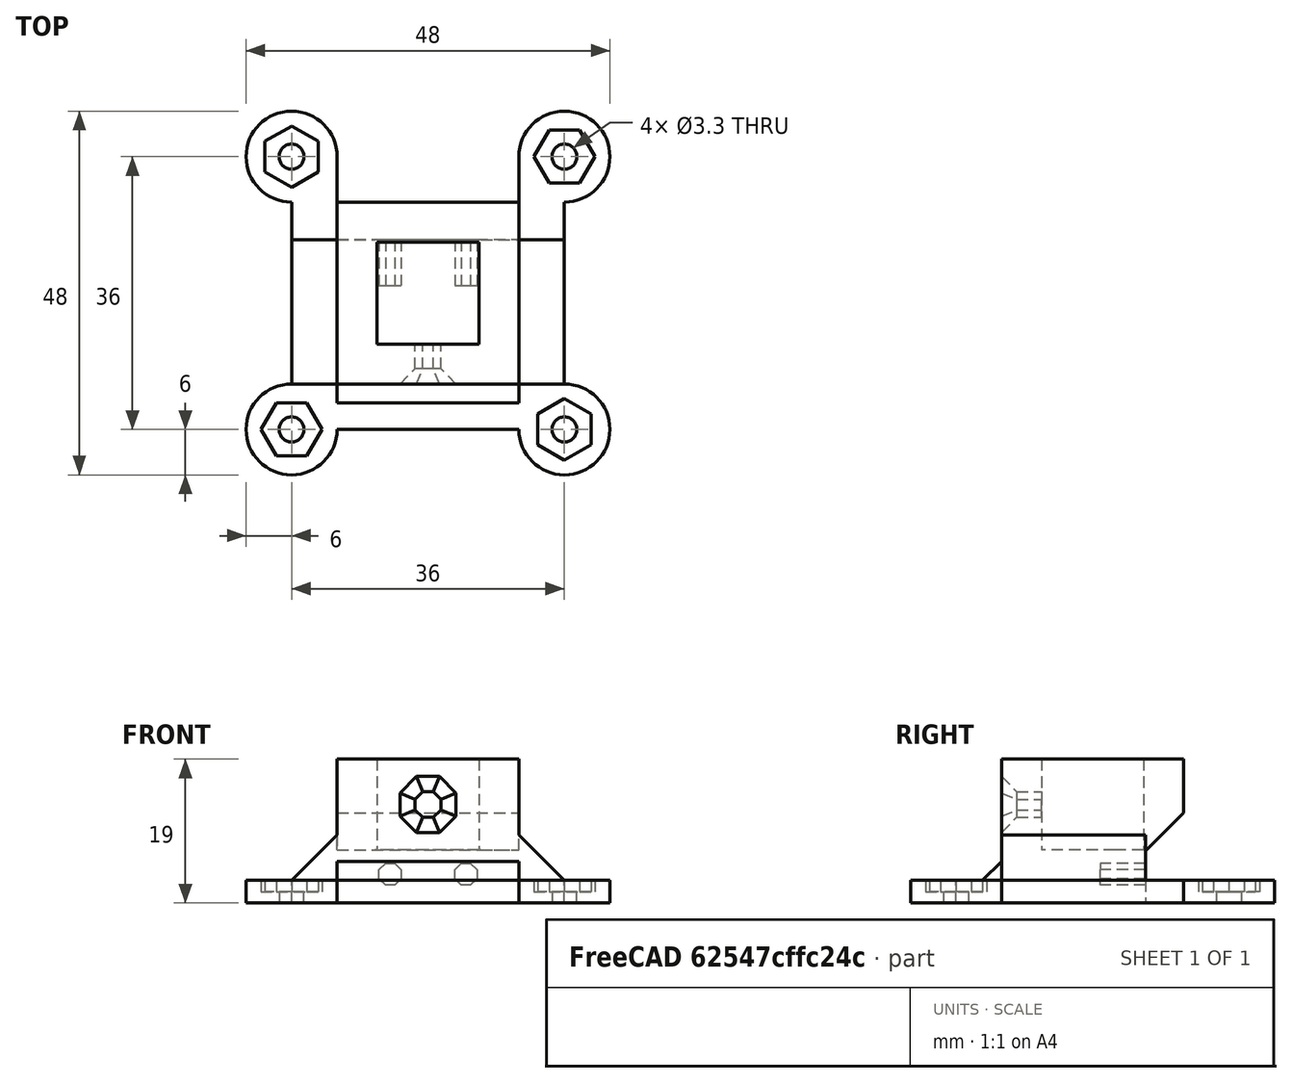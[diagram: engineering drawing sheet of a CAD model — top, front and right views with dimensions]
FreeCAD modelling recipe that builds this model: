
FCSTD DOCUMENT  (FreeCAD 0.17R13634 (Git))
Label: SG5010SquareBase V11
Comment: V6: Reinforcement at the base, following a break\n   Servo attachment octogon: 3.0 -> 3.2 mm to avoid cracks
License: CC-BY 3.0
LicenseURL: http://creativecommons.org/licenses/by/3.0/
objects: Sketcher::SketchObject×19, PartDesign::Pocket×10, PartDesign::Pad×8, PartDesign::Chamfer×5, PartDesign::Mirrored×2, PartDesign::PolarPattern×1, PartDesign::Body×1, App::Part×1
note: 64 computed .brp shape members not serialized (recipe doc carries the construction recipe); baked Part::Feature solids carry a one-line shape summary decoded from their .brp

FEATURE [Sketcher::SketchObject] Sketch  label="Base holes"
  MapMode = 5
  Support = -> [XY_Plane001]
  sketch-geometry (13):
    g0: Circle CenterX=-18 CenterY=18 CenterZ=0 NormalX=0 NormalY=0 NormalZ=1 AngleXU=0 Radius=1.65
    g1: Circle CenterX=18 CenterY=18 CenterZ=0 NormalX=0 NormalY=0 NormalZ=1 AngleXU=0 Radius=1.65
    g2: Circle CenterX=-18 CenterY=-18 CenterZ=0 NormalX=0 NormalY=0 NormalZ=1 AngleXU=0 Radius=1.65
    g3: Circle CenterX=18 CenterY=-18 CenterZ=0 NormalX=0 NormalY=0 NormalZ=1 AngleXU=0 Radius=1.65
    g4: LineSegment [constr] StartX=-18 StartY=18 StartZ=0 EndX=0 EndY=0 EndZ=0
    g5: LineSegment StartX=-12 StartY=18 StartZ=0 EndX=12 EndY=18 EndZ=0
    g6: LineSegment StartX=18 StartY=12 StartZ=0 EndX=18 EndY=-12 EndZ=0
    g7: LineSegment StartX=12 StartY=-18 StartZ=0 EndX=-12 EndY=-18 EndZ=0
    g8: LineSegment StartX=-18 StartY=-12 StartZ=0 EndX=-18 EndY=12 EndZ=0
    g9: ArcOfCircle CenterX=-18 CenterY=18 CenterZ=0 NormalX=0 NormalY=0 NormalZ=1 AngleXU=0 Radius=6 StartAngle=0 EndAngle=4.71239
    g10: ArcOfCircle CenterX=18 CenterY=18 CenterZ=0 NormalX=0 NormalY=0 NormalZ=1 AngleXU=0 Radius=6 StartAngle=4.71239 EndAngle=9.42478
    g11: ArcOfCircle CenterX=18 CenterY=-18 CenterZ=0 NormalX=0 NormalY=0 NormalZ=1 AngleXU=0 Radius=6 StartAngle=3.14159 EndAngle=7.85398
    g12: ArcOfCircle CenterX=-18 CenterY=-18 CenterZ=0 NormalX=0 NormalY=0 NormalZ=1 AngleXU=0 Radius=6 StartAngle=1.5708 EndAngle=6.28319
  constraints (35):
    c: Symmetric(g0,g1,g-2)
    c: Symmetric(g1,g3,g-1)
    c: Symmetric(g0,g2,g-1)
    c: Equal(g0,g1)
    c: Equal(g1,g3)
    c: Equal(g3,g2)
    c: Coincident(g4,g0)
    c: Coincident(g4,g-1)
    c: Angle(g4) = -0.785398
    c: Distance(g0,g1) = 36
    c: Radius(g1) = 1.65
    c: Horizontal(g5)
    c: Vertical(g6)
    c: Horizontal(g7)
    c: Vertical(g8)
    c: Coincident(g9,g5)
    c: Coincident(g9,g8)
    c: Coincident(g10,g1)
    c: Coincident(g10,g5)
    c: Coincident(g6,g10)
    c: Coincident(g11,g3)
    c: Coincident(g11,g6)
    c: Coincident(g11,g7)
    c: Coincident(g12,g2)
    c: Coincident(g7,g12)
    c: Coincident(g8,g12)
    c: Equal(g9,g10)
    c: Equal(g10,g11)
    c: Equal(g11,g12)
    c: DistanceX(g0,g8) = 0
    c: DistanceY(g7,g2) = 0
    c: DistanceX(g3,g6) = 0
    c: Coincident(g0,g9)
    c: DistanceY(g5,g0) = 0
    c: Radius(g10) = 6
FEATURE [PartDesign::Pad] Pad  label="Pad - Base holes"
  Length = 3
  Length2 = 100
  Profile = -> Sketch
  Type = 0
FEATURE [Sketcher::SketchObject] Sketch001  label="Main axis base"
  MapMode = 5
  Placement = pos=(0,0,3) rot=(0,0,1;0rad)
  Support = -> [Pad]
  sketch-geometry (4):
    g0: LineSegment StartX=-7 StartY=7 StartZ=0 EndX=7 EndY=7 EndZ=0
    g1: LineSegment StartX=7 StartY=7 StartZ=0 EndX=7 EndY=-7 EndZ=0
    g2: LineSegment StartX=7 StartY=-7 StartZ=0 EndX=-7 EndY=-7 EndZ=0
    g3: LineSegment StartX=-7 StartY=-7 StartZ=0 EndX=-7 EndY=7 EndZ=0
  constraints (12):
    c: Coincident(g0,g1)
    c: Coincident(g1,g2)
    c: Coincident(g2,g3)
    c: Coincident(g3,g0)
    c: Horizontal(g0)
    c: Horizontal(g2)
    c: Vertical(g1)
    c: Vertical(g3)
    c: Symmetric(g0,g0,g-2)
    c: Symmetric(g0,g1,g-1)
    c: Equal(g0,g1)
    c: Distance(g1) = 14
FEATURE [PartDesign::Pad] Pad001  label="Pad - Main axis base"
  BaseFeature = -> Pad
  Length = 12
  Length2 = 100
  Profile = -> Sketch001
  Type = 0
FEATURE [Sketcher::SketchObject] Sketch002  label="Main axis hole"
  MapMode = 5
  Placement = pos=(0,0,15) rot=(0,0,1;0rad)
  Support = -> [Pad001]
  sketch-geometry (1):
    g0: Circle CenterX=0 CenterY=0 CenterZ=0 NormalX=0 NormalY=0 NormalZ=1 AngleXU=0 Radius=5
  constraints (2):
    c: Coincident(g0,g-1)
    c: Radius(g0) = 5
FEATURE [PartDesign::Pocket] Pocket  label="Pocket - Main axis hole"
  BaseFeature = -> Pad001
  Length = 12
  Length2 = 100
  Profile = -> Sketch002
  Type = 0
FEATURE [Sketcher::SketchObject] Sketch003  label="Servo attachment opening"
  ExternalGeometry = -> [Pocket]
  MapMode = 5
  Placement = pos=(0,0,3) rot=(0,0,1;0rad)
  Support = -> [Pocket]
  sketch-geometry (4):
    g0: LineSegment StartX=-12 StartY=18 StartZ=0 EndX=12 EndY=18 EndZ=0
    g1: LineSegment StartX=12 StartY=18 StartZ=0 EndX=12 EndY=7 EndZ=0
    g2: LineSegment StartX=12 StartY=7 StartZ=0 EndX=-12 EndY=7 EndZ=0
    g3: LineSegment StartX=-12 StartY=7 StartZ=0 EndX=-12 EndY=18 EndZ=0
  constraints (11):
    c: Coincident(g0,g1)
    c: Coincident(g1,g2)
    c: Coincident(g2,g3)
    c: Coincident(g3,g0)
    c: Horizontal(g0)
    c: Horizontal(g2)
    c: Vertical(g1)
    c: Vertical(g3)
    c: Symmetric(g2,g1,g-2)
    c: Distance(g1) = 11
    c: Coincident(g0,g-3)
FEATURE [PartDesign::Pocket] Pocket001  label="Pocket - Servo attachment opening"
  BaseFeature = -> Pocket
  Length = 5
  Length2 = 100
  Profile = -> Sketch003
  Type = 1
FEATURE [Sketcher::SketchObject] Sketch004  label="Servo attachment wall"
  ExternalGeometry = -> [Pocket001]
  MapMode = 5
  Placement = pos=(0,7,0) rot=(0,0.707107,0.707107;3.14159rad)
  Support = -> [Pocket001]
  sketch-geometry (4):
    g0: LineSegment StartX=12 StartY=0 StartZ=0 EndX=-12 EndY=0 EndZ=0
    g1: LineSegment StartX=-12 StartY=0 StartZ=0 EndX=-12 EndY=7 EndZ=0
    g2: LineSegment StartX=-12 StartY=7 StartZ=0 EndX=12 EndY=7 EndZ=0
    g3: LineSegment StartX=12 StartY=7 StartZ=0 EndX=12 EndY=0 EndZ=0
  constraints (11):
    c: Coincident(g0,g1)
    c: Coincident(g1,g2)
    c: Coincident(g2,g3)
    c: Coincident(g3,g0)
    c: Horizontal(g0)
    c: Horizontal(g2)
    c: Vertical(g1)
    c: Vertical(g3)
    c: Coincident(g0,g-3)
    c: Coincident(g0,g-4)
    c: Distance(g1) = 7
FEATURE [PartDesign::Pad] Pad002  label="Pad - Servo attachment wall"
  BaseFeature = -> Pocket001
  Length = 2
  Length2 = 100
  Profile = -> Sketch004
  Reversed = true
  Type = 0
FEATURE [Sketcher::SketchObject] Sketch005  label="Servo attachment octogon"
  ExternalGeometry = -> [Pad002]
  MapMode = 5
  Placement = pos=(0,7,0) rot=(0,0.707107,0.707107;3.14159rad)
  Support = -> [Pad002]
  sketch-geometry (13):
    g0: LineSegment StartX=-5.66274 StartY=2.2 StartZ=0 EndX=-4.33726 EndY=2.2 EndZ=0
    g1: LineSegment StartX=-4.33726 StartY=2.2 StartZ=0 EndX=-3.4 EndY=3.13726 EndZ=0
    g2: LineSegment StartX=-3.4 StartY=3.13726 StartZ=0 EndX=-3.4 EndY=4.46274 EndZ=0
    g3: LineSegment StartX=-3.4 StartY=4.46274 StartZ=0 EndX=-4.33726 EndY=5.4 EndZ=0
    g4: LineSegment StartX=-4.33726 StartY=5.4 StartZ=0 EndX=-5.66274 EndY=5.4 EndZ=0
    g5: LineSegment StartX=-5.66274 StartY=5.4 StartZ=0 EndX=-6.6 EndY=4.46274 EndZ=0
    g6: LineSegment StartX=-6.6 StartY=4.46274 StartZ=0 EndX=-6.6 EndY=3.13726 EndZ=0
    g7: LineSegment StartX=-6.6 StartY=3.13726 StartZ=0 EndX=-5.66274 EndY=2.2 EndZ=0
    g8: LineSegment [constr] StartX=-5.66274 StartY=5.4 StartZ=0 EndX=-4.33726 EndY=2.2 EndZ=0
    g9: LineSegment [constr] StartX=-3.4 StartY=4.46274 StartZ=0 EndX=-6.6 EndY=3.13726 EndZ=0
    g10: GeomPoint [constr] X=-5 Y=3.8 Z=0
    g11: GeomPoint [constr] X=-5 Y=3.8 Z=0
    g12: GeomPoint [constr] X=5 Y=3.8 Z=0
  constraints (32):
    c: Horizontal(g0)
    c: Coincident(g0,g1)
    c: Coincident(g1,g2)
    c: Vertical(g2)
    c: Coincident(g2,g3)
    c: Coincident(g3,g4)
    c: Horizontal(g4)
    c: Coincident(g4,g5)
    c: Coincident(g5,g6)
    c: Vertical(g6)
    c: Coincident(g6,g7)
    c: Coincident(g7,g0)
    c: Equal(g5,g4)
    c: Equal(g4,g3)
    c: Equal(g3,g2)
    c: Equal(g2,g1)
    c: Equal(g1,g0)
    c: Equal(g0,g7)
    c: Equal(g7,g6)
    c: Angle(g6,g5) = 2.35619
    c: Angle(g4,g3) = 2.35619
    c: Coincident(g8,g4)
    c: Coincident(g8,g0)
    c: Coincident(g9,g2)
    c: Coincident(g9,g6)
    c: PointOnObject(g10,g8)
    c: PointOnObject(g10,g9)
    c: Distance(g5,g2) = 3.2
    c: Symmetric(g11,g12,g-2)
    c: Distance(g11,g12) = 10
    c: DistanceY(g-1,g12) = 3.8
    c: Coincident(g10,g11)
FEATURE [PartDesign::Pocket] Pocket002  label="Pocket - Servo attachment octogon"
  BaseFeature = -> Pad002
  Length = 4
  Length2 = 100
  Profile = -> Sketch005
  Type = 0
FEATURE [PartDesign::Mirrored] Mirrored
  BaseFeature = -> Pocket002
  MirrorPlane = -> Sketch005 [V_Axis]
  Originals = -> [Pocket002]
FEATURE [PartDesign::Chamfer] Chamfer
  Base = -> Mirrored [Edge55,Edge64]
  BaseFeature = -> Mirrored
  Size = 4
FEATURE [Sketcher::SketchObject] Sketch006  label="Hexagon"
  ExternalGeometry = -> [Chamfer]
  MapMode = 5
  Placement = pos=(0,0,3) rot=(0,0,1;0rad)
  Support = -> [Chamfer]
  sketch-geometry (9):
    g0: LineSegment StartX=-18 StartY=22.0415 StartZ=0 EndX=-21.5 EndY=20.0207 EndZ=0
    g1: LineSegment StartX=-21.5 StartY=20.0207 StartZ=0 EndX=-21.5 EndY=15.9793 EndZ=0
    g2: LineSegment StartX=-21.5 StartY=15.9793 StartZ=0 EndX=-18 EndY=13.9585 EndZ=0
    g3: LineSegment StartX=-18 StartY=13.9585 StartZ=0 EndX=-14.5 EndY=15.9793 EndZ=0
    g4: LineSegment StartX=-14.5 StartY=15.9793 StartZ=0 EndX=-14.5 EndY=20.0207 EndZ=0
    g5: LineSegment StartX=-14.5 StartY=20.0207 StartZ=0 EndX=-18 EndY=22.0415 EndZ=0
    g6: LineSegment [constr] StartX=-21.5 StartY=20.0207 StartZ=0 EndX=-14.5 EndY=15.9793 EndZ=0
    g7: LineSegment [constr] StartX=-14.5 StartY=20.0207 StartZ=0 EndX=-21.5 EndY=15.9793 EndZ=0
    g8: GeomPoint [constr] X=-18 Y=18 Z=0
  constraints (23):
    c: Coincident(g0,g1)
    c: Vertical(g1)
    c: Coincident(g1,g2)
    c: Coincident(g2,g3)
    c: Coincident(g3,g4)
    c: Vertical(g4)
    c: Coincident(g4,g5)
    c: Coincident(g5,g0)
    c: Equal(g0,g5)
    c: Equal(g5,g4)
    c: Equal(g4,g3)
    c: Equal(g3,g2)
    c: Equal(g2,g1)
    c: Angle(g1,g0) = 2.0944
    c: Angle(g5,g4) = 2.0944
    c: Distance(g0,g4) = 7
    c: Coincident(g6,g0)
    c: Coincident(g6,g3)
    c: Coincident(g7,g4)
    c: Coincident(g7,g1)
    c: PointOnObject(g8,g7)
    c: PointOnObject(g8,g6)
    c: Coincident(g8,g-3)
FEATURE [PartDesign::Pocket] Pocket003  label="Pocket - Hexagon"
  BaseFeature = -> Chamfer
  Length = 1.5
  Length2 = 100
  Profile = -> Sketch006
  Type = 0
FEATURE [PartDesign::PolarPattern] PolarPattern
  Angle = 360
  Axis = -> Sketch006 [N_Axis]
  BaseFeature = -> Pocket003
  Occurrences = 4
  Originals = -> [Pocket003]
FEATURE [Sketcher::SketchObject] Sketch007  label="Set screw hexagon"
  ExternalGeometry = -> [PolarPattern]
  MapMode = 5
  Placement = pos=(0,-7,0) rot=(1,0,0;1.5708rad)
  Support = -> [PolarPattern]
  sketch-geometry (14):
    g0: LineSegment [constr] StartX=-7 StartY=15 StartZ=0 EndX=7 EndY=3 EndZ=0
    g1: LineSegment [constr] StartX=-7 StartY=3 StartZ=0 EndX=7 EndY=15 EndZ=0
    g2: GeomPoint [constr] X=0 Y=9 Z=0
    g3: LineSegment StartX=-1.65 StartY=9.68345 StartZ=0 EndX=-1.65 EndY=8.31655 EndZ=0
    g4: LineSegment StartX=-1.65 StartY=8.31655 StartZ=0 EndX=-0.683452 EndY=7.35 EndZ=0
    g5: LineSegment StartX=-0.683452 StartY=7.35 StartZ=0 EndX=0.683452 EndY=7.35 EndZ=0
    g6: LineSegment StartX=0.683452 StartY=7.35 StartZ=0 EndX=1.65 EndY=8.31655 EndZ=0
    g7: LineSegment StartX=1.65 StartY=8.31655 StartZ=0 EndX=1.65 EndY=9.68345 EndZ=0
    g8: LineSegment StartX=1.65 StartY=9.68345 StartZ=0 EndX=0.683452 EndY=10.65 EndZ=0
    g9: LineSegment StartX=0.683452 StartY=10.65 StartZ=0 EndX=-0.683452 EndY=10.65 EndZ=0
    g10: LineSegment StartX=-0.683452 StartY=10.65 StartZ=0 EndX=-1.65 EndY=9.68345 EndZ=0
    g11: LineSegment [constr] StartX=-0.683452 StartY=10.65 StartZ=0 EndX=0.683452 EndY=7.35 EndZ=0
    g12: LineSegment [constr] StartX=1.65 StartY=9.68345 StartZ=0 EndX=-1.65 EndY=8.31655 EndZ=0
    g13: GeomPoint [constr] X=0 Y=9 Z=0
  constraints (35):
    c: Coincident(g0,g-3)
    c: Coincident(g0,g-4)
    c: Coincident(g1,g-3)
    c: Coincident(g1,g-4)
    c: PointOnObject(g2,g1)
    c: PointOnObject(g2,g0)
    c: Vertical(g3)
    c: Coincident(g3,g4)
    c: Coincident(g4,g5)
    c: Horizontal(g5)
    c: Coincident(g5,g6)
    c: Coincident(g6,g7)
    c: Vertical(g7)
    c: Coincident(g7,g8)
    c: Coincident(g8,g9)
    c: Horizontal(g9)
    c: Coincident(g9,g10)
    c: Coincident(g10,g3)
    c: Equal(g10,g9)
    c: Equal(g9,g8)
    c: Equal(g8,g7)
    c: Equal(g7,g6)
    c: Equal(g6,g5)
    c: Equal(g5,g4)
    c: Equal(g4,g3)
    c: Angle(g10,g9) = 2.35619
    c: Angle(g8,g7) = 2.35619
    c: Coincident(g11,g9)
    c: Coincident(g11,g5)
    c: Coincident(g12,g7)
    c: Coincident(g12,g3)
    c: PointOnObject(g13,g12)
    c: PointOnObject(g13,g11)
    c: Distance(g3,g7) = 3.3
    c: Coincident(g13,g2)
FEATURE [PartDesign::Pocket] Pocket004  label="Pocket - Set screw hexagon"
  BaseFeature = -> PolarPattern
  Length = 5
  Length2 = 100
  Profile = -> Sketch007
  Type = 0
FEATURE [PartDesign::Chamfer] Chamfer001
  Base = -> Pocket004 [Edge147,Edge60,Edge67,Edge66,Edge65,Edge64,Edge63,Edge62,Edge61]
  BaseFeature = -> Pocket004
  Size = 1
FEATURE [Sketcher::SketchObject] Sketch008  label="Rectangular base enlargement"
  ExternalGeometry = -> [Chamfer001]
  MapMode = 5
  Placement = pos=(7,0,0) rot=(0.57735,0.57735,0.57735;2.0944rad)
  Support = -> [Chamfer001]
  sketch-geometry (8):
    g0: LineSegment StartX=-7 StartY=7 StartZ=0 EndX=-12 EndY=7 EndZ=0
    g1: LineSegment StartX=-12 StartY=7 StartZ=0 EndX=-12 EndY=-12 EndZ=0
    g2: LineSegment StartX=-12 StartY=-12 StartZ=0 EndX=12 EndY=-12 EndZ=0
    g3: LineSegment StartX=12 StartY=-12 StartZ=0 EndX=12 EndY=7 EndZ=0
    g4: LineSegment StartX=12 StartY=7 StartZ=0 EndX=7 EndY=7 EndZ=0
    g5: LineSegment StartX=7 StartY=7 StartZ=0 EndX=7 EndY=-7 EndZ=0
    g6: LineSegment StartX=7 StartY=-7 StartZ=0 EndX=-7 EndY=-7 EndZ=0
    g7: LineSegment StartX=-7 StartY=-7 StartZ=0 EndX=-7 EndY=7 EndZ=0
  constraints (19):
    c: Coincident(g-3,g0)
    c: Coincident(g0,g1)
    c: Vertical(g1)
    c: Coincident(g1,g2)
    c: Horizontal(g2)
    c: Coincident(g2,g3)
    c: Vertical(g3)
    c: Coincident(g3,g4)
    c: Coincident(g4,g-4)
    c: Horizontal(g4)
    c: Coincident(g4,g5)
    c: Coincident(g5,g-4)
    c: Coincident(g5,g6)
    c: Coincident(g6,g-3)
    c: Coincident(g6,g7)
    c: Coincident(g7,g0)
    c: Symmetric(g0,g3,g-2)
    c: Coincident(g3,g-5)
    c: Distance(g3) = 19
FEATURE [PartDesign::Pad] Pad003  label="Pad - Rectangular base enlargement"
  BaseFeature = -> Chamfer001
  Length = 15
  Length2 = 100
  Profile = -> Sketch008
  Reversed = true
  Type = 0
FEATURE [Sketcher::SketchObject] Sketch009  label="Window to set screw"
  ExternalGeometry = -> [Pad003]
  MapMode = 5
  Placement = pos=(7,0,0) rot=(0.57735,0.57735,0.57735;2.0944rad)
  Support = -> [Pad003]
  sketch-geometry (10):
    g0: LineSegment [constr] StartX=-12 StartY=15 StartZ=0 EndX=12 EndY=3 EndZ=0
    g1: LineSegment [constr] StartX=-12 StartY=3 StartZ=0 EndX=12 EndY=15 EndZ=0
    g2: GeomPoint [constr] X=0 Y=9 Z=0
    g3: LineSegment StartX=-3.25 StartY=12.25 StartZ=0 EndX=3.25 EndY=12.25 EndZ=0
    g4: LineSegment StartX=3.25 StartY=12.25 StartZ=0 EndX=3.25 EndY=5.75 EndZ=0
    g5: LineSegment StartX=3.25 StartY=5.75 StartZ=0 EndX=-3.25 EndY=5.75 EndZ=0
    g6: LineSegment StartX=-3.25 StartY=5.75 StartZ=0 EndX=-3.25 EndY=12.25 EndZ=0
    g7: LineSegment [constr] StartX=-3.25 StartY=12.25 StartZ=0 EndX=3.25 EndY=5.75 EndZ=0
    g8: LineSegment [constr] StartX=3.25 StartY=12.25 StartZ=0 EndX=-3.25 EndY=5.75 EndZ=0
    g9: GeomPoint [constr] X=0 Y=9 Z=0
  constraints (23):
    c: Coincident(g0,g-4)
    c: Coincident(g0,g-3)
    c: Coincident(g1,g-4)
    c: Coincident(g1,g-3)
    c: PointOnObject(g2,g1)
    c: PointOnObject(g2,g0)
    c: Coincident(g3,g4)
    c: Coincident(g4,g5)
    c: Coincident(g5,g6)
    c: Coincident(g6,g3)
    c: Horizontal(g3)
    c: Horizontal(g5)
    c: Vertical(g4)
    c: Vertical(g6)
    c: Coincident(g7,g4)
    c: Coincident(g7,g3)
    c: Coincident(g8,g3)
    c: Coincident(g8,g5)
    c: PointOnObject(g9,g7)
    c: PointOnObject(g9,g8)
    c: Coincident(g9,g2)
    c: Equal(g3,g4)
    c: Distance(g3) = 6.5
FEATURE [PartDesign::Pocket] Pocket005
  BaseFeature = -> Pad003
  Length = 5
  Length2 = 100
  Profile = -> Sketch009
  Type = 0
FEATURE [PartDesign::Chamfer] Chamfer002
  Base = -> Pocket005 [Edge110]
  BaseFeature = -> Pocket005
  Size = 2.5
FEATURE [Sketcher::SketchObject] Sketch010  label="Side reinforcement triangle"
  ExternalGeometry = -> [Chamfer002]
  MapMode = 5
  Placement = pos=(0,7,0) rot=(0,0.707107,0.707107;3.14159rad)
  Support = -> [Chamfer002]
  sketch-geometry (3):
    g0: LineSegment StartX=12 StartY=9 StartZ=0 EndX=12 EndY=3 EndZ=0
    g1: LineSegment StartX=12 StartY=3 StartZ=0 EndX=18 EndY=3 EndZ=0
    g2: LineSegment StartX=18 StartY=3 StartZ=0 EndX=12 EndY=9 EndZ=0
  constraints (9):
    c: Vertical(g0)
    c: Coincident(g0,g1)
    c: Horizontal(g1)
    c: Coincident(g1,g2)
    c: Coincident(g2,g0)
    c: PointOnObject(g0,g-3)
    c: Coincident(g-4,g0)
    c: Distance(g1) = 6
    c: Equal(g0,g1)
FEATURE [PartDesign::Pad] Pad004  label="Pad - Side reinforcement triangle"
  BaseFeature = -> Chamfer002
  Length = 19
  Length2 = 100
  Profile = -> Sketch010
  Reversed = true
  Type = 0
FEATURE [PartDesign::Mirrored] Mirrored001
  BaseFeature = -> Pad004
  MirrorPlane = -> Sketch010 [V_Axis]
  Originals = -> [Pad004]
FEATURE [Sketcher::SketchObject] Sketch011
  MapMode = 5
  Support = -> [XY_Plane001]
FEATURE [Sketcher::SketchObject] Sketch012  label="Shave_top"
  ExternalGeometry = -> [Mirrored001]
  MapMode = 5
  Placement = pos=(0,7,0) rot=(0,0.707107,0.707107;3.14159rad)
  Support = -> [Mirrored001]
  sketch-geometry (4):
    g0: LineSegment StartX=-12 StartY=15 StartZ=0 EndX=12 EndY=15 EndZ=0
    g1: LineSegment StartX=12 StartY=15 StartZ=0 EndX=12 EndY=7 EndZ=0
    g2: LineSegment StartX=12 StartY=7 StartZ=0 EndX=-12 EndY=7 EndZ=0
    g3: LineSegment StartX=-12 StartY=7 StartZ=0 EndX=-12 EndY=15 EndZ=0
  constraints (10):
    c: Coincident(g0,g1)
    c: Coincident(g1,g2)
    c: Coincident(g2,g3)
    c: Coincident(g3,g0)
    c: Horizontal(g0)
    c: Horizontal(g2)
    c: Vertical(g1)
    c: Vertical(g3)
    c: Coincident(g-5,g0)
    c: Coincident(g1,g-6)
FEATURE [PartDesign::Pocket] Pocket006
  BaseFeature = -> Mirrored001
  Length = 5
  Length2 = 100
  Profile = -> Sketch012
  Type = 1
FEATURE [Sketcher::SketchObject] Sketch013  label="Fill_holes"
  ExternalGeometry = -> [Pocket006]
  MapMode = 5
  Placement = pos=(0,0,7) rot=(0,0,1;0rad)
  Support = -> [Pocket006]
  sketch-geometry (8):
    g0: LineSegment StartX=-4.4828 StartY=3.78315 StartZ=0 EndX=-1.67 EndY=5.48969 EndZ=0
    g1: LineSegment StartX=-1.67 StartY=5.48969 StartZ=0 EndX=1.67 EndY=5.48969 EndZ=0
    g2: LineSegment StartX=1.67 StartY=5.48969 StartZ=0 EndX=4.4828 EndY=3.78315 EndZ=0
    g3: LineSegment StartX=4.4828 StartY=3.78315 StartZ=0 EndX=6.25136 EndY=-1.53024 EndZ=0
    g4: LineSegment StartX=6.25136 StartY=-1.53024 StartZ=0 EndX=5.6 EndY=-12 EndZ=0
    g5: LineSegment StartX=5.6 StartY=-12 StartZ=0 EndX=-5.6 EndY=-12 EndZ=0
    g6: LineSegment StartX=-5.6 StartY=-12 StartZ=0 EndX=-6.25136 EndY=-1.53024 EndZ=0
    g7: LineSegment StartX=-6.25136 StartY=-1.53024 StartZ=0 EndX=-4.4828 EndY=3.78315 EndZ=0
  constraints (22):
    c: Coincident(g0,g1)
    c: Horizontal(g1)
    c: Coincident(g1,g2)
    c: Coincident(g2,g3)
    c: Coincident(g3,g4)
    c: Coincident(g4,g5)
    c: Horizontal(g5)
    c: Coincident(g5,g6)
    c: Coincident(g6,g7)
    c: Coincident(g7,g0)
    c: PointOnObject(g4,g-5)
    c: Symmetric(g0,g1,g-2)
    c: Symmetric(g0,g2,g-2)
    c: Symmetric(g6,g3,g-2)
    c: Symmetric(g5,g4,g-2)
    c: Distance(g5) = 11.2
    c: Distance(g6) = 10.49
    c: Distance(g7) = 5.6
    c: Distance(g0) = 3.29
    c: Distance(g1) = 3.34
    c: Angle(g3) = -1.24948
    c: Angle(g4) = -1.63293
FEATURE [PartDesign::Pad] Pad005
  BaseFeature = -> Pocket006
  Length = 7
  Length2 = 100
  Profile = -> Sketch013
  Reversed = true
  Type = 0
FEATURE [Sketcher::SketchObject] Sketch014  label="SquareBase"
  ExternalGeometry = -> [Pad005]
  MapMode = 5
  Placement = pos=(0,0,7) rot=(0,0,1;0rad)
  Support = -> [Pad005]
  sketch-geometry (4):
    g0: LineSegment StartX=12 StartY=-12 StartZ=0 EndX=-12 EndY=-12 EndZ=0
    g1: LineSegment StartX=-12 StartY=-12 StartZ=0 EndX=-12 EndY=12 EndZ=0
    g2: LineSegment StartX=-12 StartY=12 StartZ=0 EndX=12 EndY=12 EndZ=0
    g3: LineSegment StartX=12 StartY=12 StartZ=0 EndX=12 EndY=-12 EndZ=0
  constraints (11):
    c: Coincident(g0,g1)
    c: Coincident(g1,g2)
    c: Coincident(g2,g3)
    c: Coincident(g3,g0)
    c: Horizontal(g0)
    c: Horizontal(g2)
    c: Vertical(g1)
    c: Vertical(g3)
    c: Coincident(g0,g-4)
    c: PointOnObject(g-3,g1)
    c: Symmetric(g2,g0,g-1)
FEATURE [PartDesign::Pad] Pad006
  BaseFeature = -> Pad005
  Length = 12
  Length2 = 100
  Profile = -> Sketch014
  Type = 0
FEATURE [Sketcher::SketchObject] Sketch015  label="SquareHole"
  MapMode = 5
  Placement = pos=(0,0,19) rot=(0,0,1;0rad)
  Support = -> [Pad006]
  sketch-geometry (6):
    g0: LineSegment StartX=-6.725 StartY=6.725 StartZ=0 EndX=6.725 EndY=6.725 EndZ=0
    g1: LineSegment StartX=6.725 StartY=6.725 StartZ=0 EndX=6.725 EndY=-6.725 EndZ=0
    g2: LineSegment StartX=6.725 StartY=-6.725 StartZ=0 EndX=-6.725 EndY=-6.725 EndZ=0
    g3: LineSegment StartX=-6.725 StartY=-6.725 StartZ=0 EndX=-6.725 EndY=6.725 EndZ=0
    g4: LineSegment [constr] StartX=-6.725 StartY=6.725 StartZ=0 EndX=6.725 EndY=-6.725 EndZ=0
    g5: LineSegment [constr] StartX=6.725 StartY=6.725 StartZ=0 EndX=-6.725 EndY=-6.725 EndZ=0
  constraints (16):
    c: Coincident(g0,g1)
    c: Coincident(g1,g2)
    c: Coincident(g2,g3)
    c: Coincident(g3,g0)
    c: Horizontal(g0)
    c: Horizontal(g2)
    c: Vertical(g1)
    c: Vertical(g3)
    c: Equal(g1,g2)
    c: Coincident(g4,g0)
    c: Coincident(g4,g1)
    c: Coincident(g5,g0)
    c: Coincident(g5,g2)
    c: PointOnObject(g-1,g4)
    c: PointOnObject(g-1,g5)
    c: Distance(g0) = 13.45
FEATURE [PartDesign::Pocket] Pocket007
  BaseFeature = -> Pad006
  Length = 12
  Length2 = 100
  Profile = -> Sketch015
  Type = 0
FEATURE [Sketcher::SketchObject] Sketch016  label="OctagonHole"
  ExternalGeometry = -> [Pocket007]
  MapMode = 5
  Placement = pos=(0,-12,0) rot=(1,0,0;1.5708rad)
  Support = -> [Pocket007]
  sketch-geometry (12):
    g0: LineSegment [constr] StartX=-12 StartY=19 StartZ=0 EndX=12 EndY=7 EndZ=0
    g1: LineSegment [constr] StartX=12 StartY=19 StartZ=0 EndX=-12 EndY=7 EndZ=0
    g2: GeomPoint X=0 Y=13 Z=0
    g3: LineSegment StartX=1.7 StartY=12.2958 StartZ=0 EndX=1.7 EndY=13.7042 EndZ=0
    g4: LineSegment StartX=1.7 StartY=13.7042 StartZ=0 EndX=0.704163 EndY=14.7 EndZ=0
    g5: LineSegment StartX=0.704163 StartY=14.7 StartZ=0 EndX=-0.704163 EndY=14.7 EndZ=0
    g6: LineSegment StartX=-0.704163 StartY=14.7 StartZ=0 EndX=-1.7 EndY=13.7042 EndZ=0
    g7: LineSegment StartX=-1.7 StartY=13.7042 StartZ=0 EndX=-1.7 EndY=12.2958 EndZ=0
    g8: LineSegment StartX=-1.7 StartY=12.2958 StartZ=0 EndX=-0.704163 EndY=11.3 EndZ=0
    g9: LineSegment StartX=-0.704163 StartY=11.3 StartZ=0 EndX=0.704163 EndY=11.3 EndZ=0
    g10: LineSegment StartX=0.704163 StartY=11.3 StartZ=0 EndX=1.7 EndY=12.2958 EndZ=0
    g11: Circle [constr] CenterX=0 CenterY=13 CenterZ=0 NormalX=0 NormalY=0 NormalZ=1 AngleXU=0 Radius=1.84007
  constraints (26):
    c: Coincident(g0,g-5)
    c: Coincident(g0,g-3)
    c: Coincident(g1,g-4)
    c: Coincident(g1,g-6)
    c: PointOnObject(g2,g1)
    c: PointOnObject(g2,g0)
    c: Coincident(g3,g4)
    c: Coincident(g4,g5)
    c: Coincident(g5,g6)
    c: Coincident(g6,g7)
    c: Coincident(g7,g8)
    c: Coincident(g8,g9)
    c: Coincident(g9,g10)
    c: Coincident(g10,g3)
    c: Equal(g3, g4-g10) x7
    c: PointOnObject(g3,g11)
    c: PointOnObject(g4,g11)
    c: PointOnObject(g5,g11)
    c: PointOnObject(g6,g11)
    c: PointOnObject(g7,g11)
    c: PointOnObject(g8,g11)
    c: PointOnObject(g9,g11)
    c: PointOnObject(g10,g11)
    c: Coincident(g11,g2)
    c: Horizontal(g5)
    c: Distance(g6,g3) = 3.4
FEATURE [PartDesign::Pocket] Pocket008
  BaseFeature = -> Pocket007
  Length = 7
  Length2 = 100
  Profile = -> Sketch016
  Type = 0
FEATURE [PartDesign::Chamfer] Chamfer003
  Base = -> Pocket008 [Edge139,Edge138,Edge145,Edge144,Edge143,Edge142,Edge140,Edge141]
  BaseFeature = -> Pocket008
  Size = 2
FEATURE [PartDesign::Chamfer] Chamfer004
  Base = -> Chamfer003 [Edge104]
  BaseFeature = -> Chamfer003
  Size = 4.9
FEATURE [Sketcher::SketchObject] Sketch017  label="FillScrewHoles"
  ExternalGeometry = -> [Chamfer004]
  MapMode = 5
  Placement = pos=(0,7,0) rot=(0,0.707107,0.707107;3.14159rad)
  Support = -> [Chamfer004]
  sketch-geometry (4):
    g0: LineSegment StartX=-7 StartY=7 StartZ=0 EndX=7 EndY=7 EndZ=0
    g1: LineSegment StartX=7 StartY=7 StartZ=0 EndX=7 EndY=0 EndZ=0
    g2: LineSegment StartX=7 StartY=0 StartZ=0 EndX=-7 EndY=0 EndZ=0
    g3: LineSegment StartX=-7 StartY=0 StartZ=0 EndX=-7 EndY=7 EndZ=0
  constraints (10):
    c: Coincident(g0,g1)
    c: Coincident(g1,g2)
    c: Coincident(g2,g3)
    c: Coincident(g3,g0)
    c: Horizontal(g0)
    c: Horizontal(g2)
    c: Vertical(g1)
    c: Vertical(g3)
    c: Coincident(g0,g-4)
    c: Coincident(g1,g-6)
FEATURE [PartDesign::Pad] Pad007
  BaseFeature = -> Chamfer004
  Length = 4
  Length2 = 100
  Profile = -> Sketch017
  Reversed = true
  Type = 0
FEATURE [Sketcher::SketchObject] Sketch018  label="ScrewHoles"
  ExternalGeometry = -> [Pad007]
  MapMode = 5
  Placement = pos=(0,7,0) rot=(0,0.707107,0.707107;3.14159rad)
  Support = -> [Pad007]
  sketch-geometry (24):
    g0: LineSegment [constr] StartX=4.33726 StartY=5.4 StartZ=0 EndX=5.66274 EndY=2.2 EndZ=0
    g1: LineSegment [constr] StartX=5.66274 StartY=5.4 StartZ=0 EndX=4.33726 EndY=2.2 EndZ=0
    g2: LineSegment [constr] StartX=-5.66274 StartY=5.4 StartZ=0 EndX=-4.33726 EndY=2.2 EndZ=0
    g3: LineSegment [constr] StartX=-4.33726 StartY=5.4 StartZ=0 EndX=-5.66274 EndY=2.2 EndZ=0
    g4: GeomPoint X=5 Y=3.8 Z=0
    g5: GeomPoint X=-5 Y=3.8 Z=0
    g6: LineSegment StartX=5.60061 StartY=2.35 StartZ=0 EndX=6.45 EndY=3.19939 EndZ=0
    g7: LineSegment StartX=6.45 StartY=3.19939 StartZ=0 EndX=6.45 EndY=4.40061 EndZ=0
    g8: LineSegment StartX=6.45 StartY=4.40061 StartZ=0 EndX=5.60061 EndY=5.25 EndZ=0
    g9: LineSegment StartX=5.60061 StartY=5.25 StartZ=0 EndX=4.39939 EndY=5.25 EndZ=0
    g10: LineSegment StartX=4.39939 StartY=5.25 StartZ=0 EndX=3.55 EndY=4.40061 EndZ=0
    g11: LineSegment StartX=3.55 StartY=4.40061 StartZ=0 EndX=3.55 EndY=3.19939 EndZ=0
    g12: LineSegment StartX=3.55 StartY=3.19939 StartZ=0 EndX=4.39939 EndY=2.35 EndZ=0
    g13: LineSegment StartX=4.39939 StartY=2.35 StartZ=0 EndX=5.60061 EndY=2.35 EndZ=0
    g14: Circle [constr] CenterX=5 CenterY=3.8 CenterZ=0 NormalX=0 NormalY=0 NormalZ=1 AngleXU=0 Radius=1.56947
    g15: LineSegment StartX=-3.55 StartY=3.19939 StartZ=0 EndX=-3.55 EndY=4.40061 EndZ=0
    g16: LineSegment StartX=-3.55 StartY=4.40061 StartZ=0 EndX=-4.39939 EndY=5.25 EndZ=0
    g17: LineSegment StartX=-4.39939 StartY=5.25 StartZ=0 EndX=-5.60061 EndY=5.25 EndZ=0
    g18: LineSegment StartX=-5.60061 StartY=5.25 StartZ=0 EndX=-6.45 EndY=4.40061 EndZ=0
    g19: LineSegment StartX=-6.45 StartY=4.40061 StartZ=0 EndX=-6.45 EndY=3.19939 EndZ=0
    g20: LineSegment StartX=-6.45 StartY=3.19939 StartZ=0 EndX=-5.60061 EndY=2.35 EndZ=0
    g21: LineSegment StartX=-5.60061 StartY=2.35 StartZ=0 EndX=-4.39939 EndY=2.35 EndZ=0
    g22: LineSegment StartX=-4.39939 StartY=2.35 StartZ=0 EndX=-3.55 EndY=3.19939 EndZ=0
    g23: Circle [constr] CenterX=-5 CenterY=3.8 CenterZ=0 NormalX=0 NormalY=0 NormalZ=1 AngleXU=0 Radius=1.56947
  constraints (52):
    c: Coincident(g0,g-3)
    c: Coincident(g0,g-4)
    c: Coincident(g1,g-3)
    c: Coincident(g1,g-4)
    c: Coincident(g2,g-5)
    c: Coincident(g2,g-6)
    c: Coincident(g3,g-5)
    c: Coincident(g3,g-6)
    c: PointOnObject(g4,g1)
    c: PointOnObject(g4,g0)
    c: PointOnObject(g5,g3)
    c: PointOnObject(g5,g2)
    c: Coincident(g6,g7)
    c: Coincident(g7,g8)
    c: Coincident(g8,g9)
    c: Coincident(g9,g10)
    c: Coincident(g10,g11)
    c: Coincident(g11,g12)
    c: Coincident(g12,g13)
    c: Coincident(g13,g6)
    c: Equal(g6, g7-g13) x7
    c: PointOnObject(g6,g14)
    c: PointOnObject(g7,g14)
    c: PointOnObject(g8,g14)
    c: PointOnObject(g9,g14)
    c: PointOnObject(g10,g14)
    c: PointOnObject(g11,g14)
    c: PointOnObject(g12,g14)
    c: PointOnObject(g13,g14)
    c: Coincident(g4,g14)
    c: Horizontal(g9)
    c: Distance(g10,g7) = 2.9
    c: Coincident(g15,g16)
    c: Coincident(g16,g17)
    c: Coincident(g17,g18)
    c: Coincident(g18,g19)
    c: Coincident(g19,g20)
    c: Coincident(g20,g21)
    c: Coincident(g21,g22)
    c: Coincident(g22,g15)
    c: Equal(g15, g16-g22) x7
    c: PointOnObject(g15,g23)
    c: PointOnObject(g16,g23)
    c: PointOnObject(g17,g23)
    c: PointOnObject(g18,g23)
    c: PointOnObject(g19,g23)
    c: PointOnObject(g20,g23)
    c: PointOnObject(g21,g23)
    c: PointOnObject(g22,g23)
    c: Equal(g23,g14)
    c: Horizontal(g17)
    c: Coincident(g5,g23)
FEATURE [PartDesign::Pocket] Pocket009
  BaseFeature = -> Pad007
  Length = 6
  Length2 = 100
  Profile = -> Sketch018
  Type = 0
FEATURE [PartDesign::Body] Mirrored001Body
  Group = -> [Sketch,Pad,Sketch001,Pad001,Sketch002,Pocket,Sketch003,Pocket001,Sketch004,Pad002,Sketch005,Pocket002,Mirrored,Chamfer,Sketch006,Pocket003,PolarPattern,Sketch007,Pocket004,Chamfer001,Sketch008,Pad003,Sketch009,Pocket005,Chamfer002,Sketch010,Pad004,Mirrored001,Sketch011,Sketch012,Pocket006,Sketch013,Pad005,Sketch014,Pad006,Sketch015,Pocket007,Sketch016,Pocket008,Chamfer003,Chamfer004,Sketch017,+3 more]
  Origin = -> Origin001
  Tip = -> Pocket009
FEATURE [App::Part] Part
  Group = -> [Mirrored001Body]
  License = CC BY 3.0
  LicenseURL = http://creativecommons.org/licenses/by/3.0/
  Origin = -> Origin
